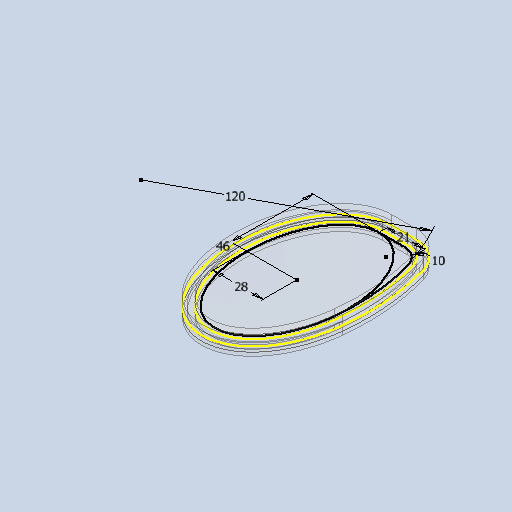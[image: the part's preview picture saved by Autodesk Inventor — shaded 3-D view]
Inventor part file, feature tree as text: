
AUTODESK INVENTOR PART (.ipt)
format: ipt  version: 2022 (Build 260153070, 153G)  size: 271,872 bytes
history: native  units: mm
features: extrude x4, sketch x3, thicken_offset x3, projected_geometry x2
ambient origin geometry x8: Origin, YZ Plane, XZ Plane, XY Plane, X Axis, Y Axis, Z Axis, Center Point
bodies: Solid1 (feature_tree), Solid3 (feature_tree), Solid4 (feature_tree), Solid5 (feature_tree)
feature tree (12):
  sketch  "Sketch1"  dims[d0=28.0mm d1=46.0mm]
  extrude  "Extrusion1"  Depth=46.0mm
  thicken_offset  "Thicken3"
  thicken_offset  "Thicken4"
  sketch  "Sketch3"  dims[d3=120.0mm d5=21.0mm]
  extrude  "Extrusion6"  Depth=21.0mm
  extrude  "Extrusion7"  Depth=2.0mm TaperAngle=0.0deg
  thicken_offset  "Thicken6"
  extrude  "Extrusion8"  Depth=2.0mm
  projected_geometry  "Projected Loop2"
  sketch  "Sketch4"  dims[d6=10.0mm d7=2.0mm d8=0.0mm d19=2.0mm d20=3.0mm d23=5.0mm d24=2.0mm d25=3.0mm d26=6.0mm d27=0.0mm d28=0.0mm d29=2.0mm d30=0.0mm d33=3.0mm d34=3.0mm d35=5.0mm d36=0.0mm]
  projected_geometry  "Projected Loop3"
